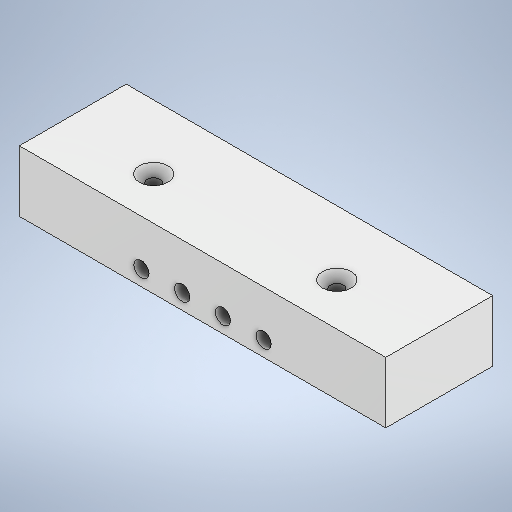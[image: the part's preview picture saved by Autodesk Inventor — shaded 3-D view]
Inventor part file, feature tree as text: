
AUTODESK INVENTOR PART (.ipt)
format: ipt  version: 2025 (Build 290162010, 162A)  size: 276,480 bytes
history: native  units: mm
features: sketch x4, hole x3, extrude x1
ambient origin geometry x8: Origin, YZ Plane, XZ Plane, XY Plane, X Axis, Y Axis, Z Axis, Center Point
bodies: Volumenkörper1 (feature_tree)
feature tree (8):
  extrude  "Extrusion1"  Depth=13.333333mm
  hole  "Bohrung1"  [1 undecoded]
  hole  "Bohrung2"  [1 undecoded]
  hole  "Bohrung3"  [1 undecoded]
  sketch  "Skizze1"  dims[d1=0.0mm d2=13.333333mm]
  sketch  "Skizze2"  dims[d3=5.0mm d5=40.0mm]
  sketch  "Skizze3"  dims[d6=1.567mm d7=8.0mm d8=4.0mm d9=2.0mm d10=90.0deg d11=10.0mm d12=20.594885mm d14=35.0mm]
  sketch  "Skizze4"  dims[d15=120.0mm d16=5.0mm d17=6.0mm d18=4.0mm d19=2.0mm d20=90.0deg d21=8.0mm d22=20.594885mm d23=60.0mm d24=5.0mm d25=60.0mm d26=14.0mm d27=4.3mm d28=12.7mm d29=9.4mm d30=2.0mm d31=90.0deg d32=8.0mm d33=20.594885mm]
note: 3 required parameter values undecoded (feature->parameter linkage not recoverable at this tier; creation-order binding heuristic only, values carry confidence <= 0.55)
